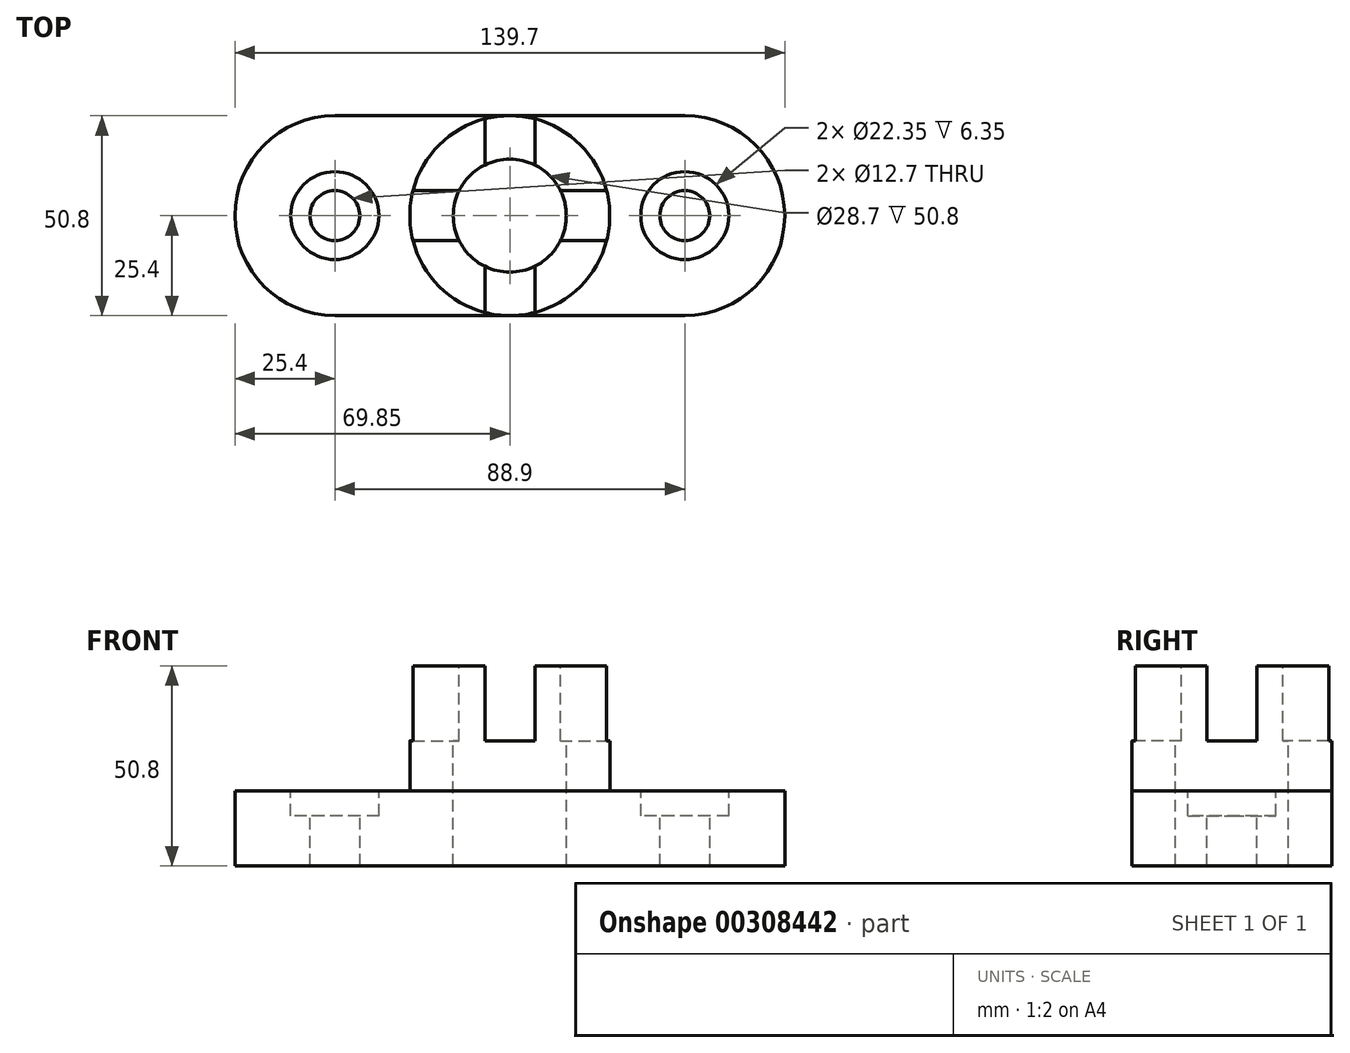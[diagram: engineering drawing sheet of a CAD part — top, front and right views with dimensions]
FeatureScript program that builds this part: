
annotation { "Feature Type Name" : "Feature", "Feature Type Description" : "" }
export const myFeature = defineFeature(function(context is Context, id is Id, definition is map)
    precondition{}
    {
        {
            var Q0;
            Q0=qCreatedBy(makeId("Top.planeOp"),FACE);
            var sketch = newSketch(context, id + "F0", { "sketchPlane" : qUnion([Q0])});
            skLineSegment(sketch, "E0.bottom", {"start": v(-44.45, 0) * mm, "end": v(44.45, 0) * mm});
            skLineSegment(sketch, "E0.top", {"start": v(-44.45, 50.8) * mm, "end": v(44.45, 50.8) * mm});
            skLineSegment(sketch, "E0.left", {"start": v(-44.45, 0) * mm, "end": v(-44.45, 50.8) * mm});
            skLineSegment(sketch, "E1", {"start": v(44.45, 0) * mm, "end": v(44.45, 0) * mm});
            skLineSegment(sketch, "E2", {"start": v(44.45, 50.8) * mm, "end": v(44.45, 0) * mm});
            skArc(sketch, "E3", {"start": v(44.45, 0) * mm, "mid": v(69.85, 25.4) * mm, "end": v(44.45, 50.8) * mm});
            skArc(sketch, "E4", {"start": v(-44.45, 50.8) * mm, "mid": v(-69.85, 25.4) * mm, "end": v(-44.45, 0) * mm});
            skSolve(sketch);
        }
        {
            var Q0;
            Q0 = qSketchRegion(id + "F0", true);
            extrude(context, id + "F1", {"entities" : qUnion([Q0]), "depth" : 19.05 * mm});
        }
        {
            var Q0;
            Q0=makeQuery(id+"F1.opExtrude","CAP_FACE",FACE,{"disambiguationData":[OSD([sQuery(id+"F0.wireOp",EDGE,"E0.bottom"),sQuery(id+"F0.wireOp",EDGE,"E0.top"),sQuery(id+"F0.wireOp",EDGE,"E3"),sQuery(id+"F0.wireOp",EDGE,"E4")])],"isStart":false});
            var sketch = newSketch(context, id + "F2", { "sketchPlane" : qUnion([Q0])});
            skCircle(sketch, "E5", {"center": v(-44.45, 25.4) * mm, "radius": 6.35 * mm});
            skCircle(sketch, "E6", {"center": v(44.45, 25.4) * mm, "radius": 6.35 * mm});
            skCircle(sketch, "E7", {"center": v(-44.45, 25.4) * mm, "radius": 11.18 * mm});
            skCircle(sketch, "E8", {"center": v(44.45, 25.4) * mm, "radius": 11.18 * mm});
            skSolve(sketch);
        }
        {
            var Q0;
            Q0 = qSketchRegion(id + "F2", true);
            extrude(context, id + "F3", {"entities" : qUnion([Q0]), "operationType" : NewBodyOperationType.REMOVE, "oppositeDirection" : true, "depth" : 6.35 * mm});
        }
        {
            var Q0;
            Q0=makeQuery(id+"F3.boolean.opBoolean","SPLIT",FACE,{"disambiguationData":[TD([makeQuery(id+"F3.opExtrude","SWEPT_FACE",FACE,{"disambiguationData":[OSD([sQuery(id+"F2.wireOp",EDGE,"E5")])]})])],"derivedFrom":makeQuery(id+"F1.opExtrude","CAP_FACE",FACE,{"disambiguationData":[OSD([sQuery(id+"F0.wireOp",EDGE,"E0.bottom"),sQuery(id+"F0.wireOp",EDGE,"E0.top"),sQuery(id+"F0.wireOp",EDGE,"E3"),sQuery(id+"F0.wireOp",EDGE,"E4")])],"isStart":false})});
            var Q1;
            Q1=makeQuery(id+"F3.boolean.opBoolean","SPLIT",FACE,{"disambiguationData":[TD([makeQuery(id+"F3.opExtrude","SWEPT_FACE",FACE,{"disambiguationData":[OSD([sQuery(id+"F2.wireOp",EDGE,"E6")])]})])],"derivedFrom":makeQuery(id+"F1.opExtrude","CAP_FACE",FACE,{"disambiguationData":[OSD([sQuery(id+"F0.wireOp",EDGE,"E0.bottom"),sQuery(id+"F0.wireOp",EDGE,"E0.top"),sQuery(id+"F0.wireOp",EDGE,"E3"),sQuery(id+"F0.wireOp",EDGE,"E4")])],"isStart":false})});
            extrude(context, id + "F4", {"entities" : qUnion([Q0, Q1]), "operationType" : NewBodyOperationType.REMOVE, "endBound" : BoundingType.THROUGH_ALL, "oppositeDirection" : true, "depth" : 25.4 * mm});
        }
        {
            var Q0;
            {var subQ0=sQuery(id+"F0.wireOp",EDGE,"E3");var subQ1=sQuery(id+"F0.wireOp",EDGE,"E0.top");var subQ2=sQuery(id+"F0.wireOp",EDGE,"E4");var subQ3=sQuery(id+"F0.wireOp",EDGE,"E0.bottom");Q0=makeQuery(id+"F3.boolean.opBoolean","SPLIT",FACE,{"disambiguationData":[TD([makeQuery(id+"F1.opExtrude","SWEPT_FACE",FACE,{"disambiguationData":[OSD([subQ3])]})])],"derivedFrom":makeQuery(id+"F1.opExtrude","CAP_FACE",FACE,{"disambiguationData":[OSD([subQ3,subQ1,subQ0,subQ2])],"isStart":false})});}
            var sketch = newSketch(context, id + "F5", { "sketchPlane" : qUnion([Q0])});
            skCircle(sketch, "E9", {"center": v(0, 25.4) * mm, "radius": 25.4 * mm});
            skSolve(sketch);
        }
        {
            var Q0;
            Q0 = qSketchRegion(id + "F5", true);
            extrude(context, id + "F6", {"entities" : qUnion([Q0]), "operationType" : NewBodyOperationType.ADD, "depth" : 31.75 * mm});
        }
        {
            var Q0;
            Q0=makeQuery(id+"F6.opExtrude","CAP_FACE",FACE,{"disambiguationData":[OSD([sQuery(id+"F5.wireOp",EDGE,"E9")])],"isStart":false});
            var sketch = newSketch(context, id + "F7", { "sketchPlane" : qUnion([Q0])});
            skCircle(sketch, "E10", {"center": v(0, 25.4) * mm, "radius": 14.35 * mm});
            skSolve(sketch);
        }
        {
            var Q0;
            Q0 = qSketchRegion(id + "F7", true);
            extrude(context, id + "F8", {"entities" : qUnion([Q0]), "operationType" : NewBodyOperationType.REMOVE, "endBound" : BoundingType.THROUGH_ALL, "oppositeDirection" : true, "depth" : 25.4 * mm});
        }
        {
            var Q0;
            Q0=makeQuery(id+"F6.opExtrude","CAP_FACE",FACE,{"disambiguationData":[OSD([sQuery(id+"F5.wireOp",EDGE,"E9")])],"isStart":false});
            var sketch = newSketch(context, id + "F9", { "sketchPlane" : qUnion([Q0])});
            skLineSegment(sketch, "E11.bottom", {"start": v(-6.35, 50.8) * mm, "end": v(6.35, 50.8) * mm});
            skLineSegment(sketch, "E11.top", {"start": v(-6.35, 0) * mm, "end": v(6.35, 0) * mm});
            skLineSegment(sketch, "E11.left", {"start": v(-6.35, 50.8) * mm, "end": v(-6.35, 0) * mm});
            skLineSegment(sketch, "E11.right", {"start": v(6.35, 50.8) * mm, "end": v(6.35, 0) * mm});
            skSolve(sketch);
        }
        {
            var Q0;
            Q0 = qSketchRegion(id + "F9", true);
            extrude(context, id + "F10", {"entities" : qUnion([Q0]), "operationType" : NewBodyOperationType.REMOVE, "oppositeDirection" : true, "depth" : 19.05 * mm});
        }
        {
            var Q0;
            {var subQ0=sQuery(id+"F5.wireOp",EDGE,"E9");Q0=makeQuery(id+"F10.boolean.opBoolean","SPLIT",FACE,{"disambiguationData":[TD([makeQuery(id+"F10.opExtrude","SWEPT_FACE",FACE,{"disambiguationData":[OSD([sQuery(id+"F9.wireOp",EDGE,"E11.right")])]})])],"derivedFrom":makeQuery(id+"F6.opExtrude","CAP_FACE",FACE,{"disambiguationData":[OSD([subQ0])],"isStart":false})});}
            var sketch = newSketch(context, id + "F11", { "sketchPlane" : qUnion([Q0])});
            skLineSegment(sketch, "E12.bottom", {"start": v(-31.34, 31.75) * mm, "end": v(28.33, 31.75) * mm});
            skLineSegment(sketch, "E12.top", {"start": v(-31.34, 19.05) * mm, "end": v(28.33, 19.05) * mm});
            skLineSegment(sketch, "E12.left", {"start": v(-31.34, 31.75) * mm, "end": v(-31.34, 19.05) * mm});
            skLineSegment(sketch, "E12.right", {"start": v(28.33, 31.75) * mm, "end": v(28.33, 19.05) * mm});
            skSolve(sketch);
        }
        {
            var Q0;
            Q0 = qSketchRegion(id + "F11", true);
            extrude(context, id + "F12", {"entities" : qUnion([Q0]), "operationType" : NewBodyOperationType.REMOVE, "oppositeDirection" : true, "depth" : 19.05 * mm});
        }
    });
